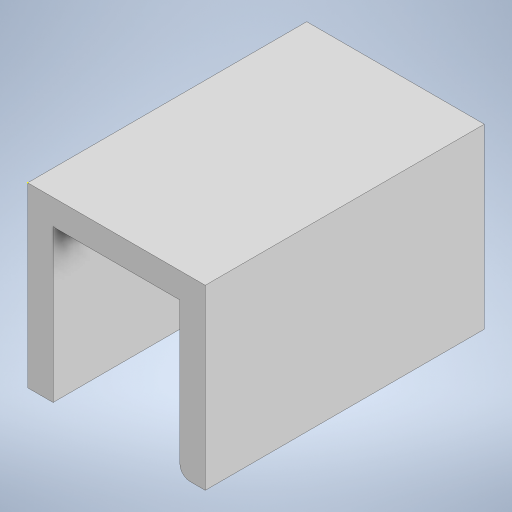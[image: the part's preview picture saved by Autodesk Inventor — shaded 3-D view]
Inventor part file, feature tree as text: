
AUTODESK INVENTOR PART (.ipt)
format: ipt  version: 2023 (Build 270158000, 158)  size: 210,944 bytes
history: native  units: in
note: dims shown in document units (in); Inventor stores cm internally (conversion verified against a paired STEP export)
features: sketch x9, extrude x4, fillet x1
ambient origin geometry x8: Origin, YZ Plane, XZ Plane, XY Plane, X Axis, Y Axis, Z Axis, Center Point
bodies: Solid1 (feature_tree)
feature tree (14):
  extrude  "Extrusion1"  Depth=0.5512in
  extrude  "Extrusion2"  Depth=0.3937in
  sketch  "Sketch8"  dims[d5=0.7874in d6=0.7874in d7=0.0in]
  sketch  "Sketch9"  dims[d30=0.1969in d31=0.4724in d32=0.0787in d33=0.0in]
  sketch  "Sketch11"  dims[d34=0.1772in]
  sketch  "Sketch14"  dims[d35=0.1772in]
  sketch  "Sketch15"  dims[d36=0.3543in d37=0.0in]
  extrude  "Extrusion10"  Depth=0.7874in TaperAngle=0.0deg
  extrude  "Extrusion11"  Depth=0.4724in
  fillet  "Fillet1"  Radius=0.0787in
  sketch  "Sketch1"  dims[d0=0.5512in d1=0.5512in]
  sketch  "Sketch2"  dims[d2=0.8661in d3=0.0in d4=0.3937in]
  sketch  "Sketch16"  dims[d38=0.0315in]
  sketch  "Sketch17"  dims[d39=0.0in d40=0.0in d41=0.0in]
